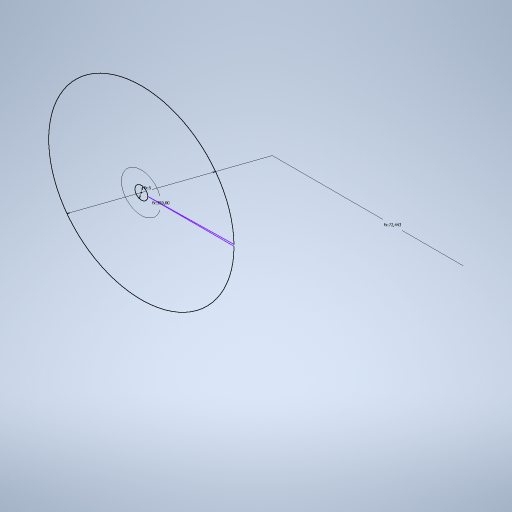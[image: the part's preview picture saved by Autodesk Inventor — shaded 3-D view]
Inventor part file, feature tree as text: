
AUTODESK INVENTOR PART (.ipt)
format: ipt  version: 2024 (Build 280153000, 153)  size: 225,792 bytes
history: native  units: mm
features: sketch x1
ambient origin geometry x8: Origin, YZ Plane, XZ Plane, XY Plane, X Axis, Y Axis, Z Axis, Center Point
feature tree (1):
  sketch  "Sketch1"  dims[d0=5.0mm d1=72.442857mm d2=62.65732mm d3=0.5mm d4=0.872665mm d5=0.5mm d6=0.872665mm]
